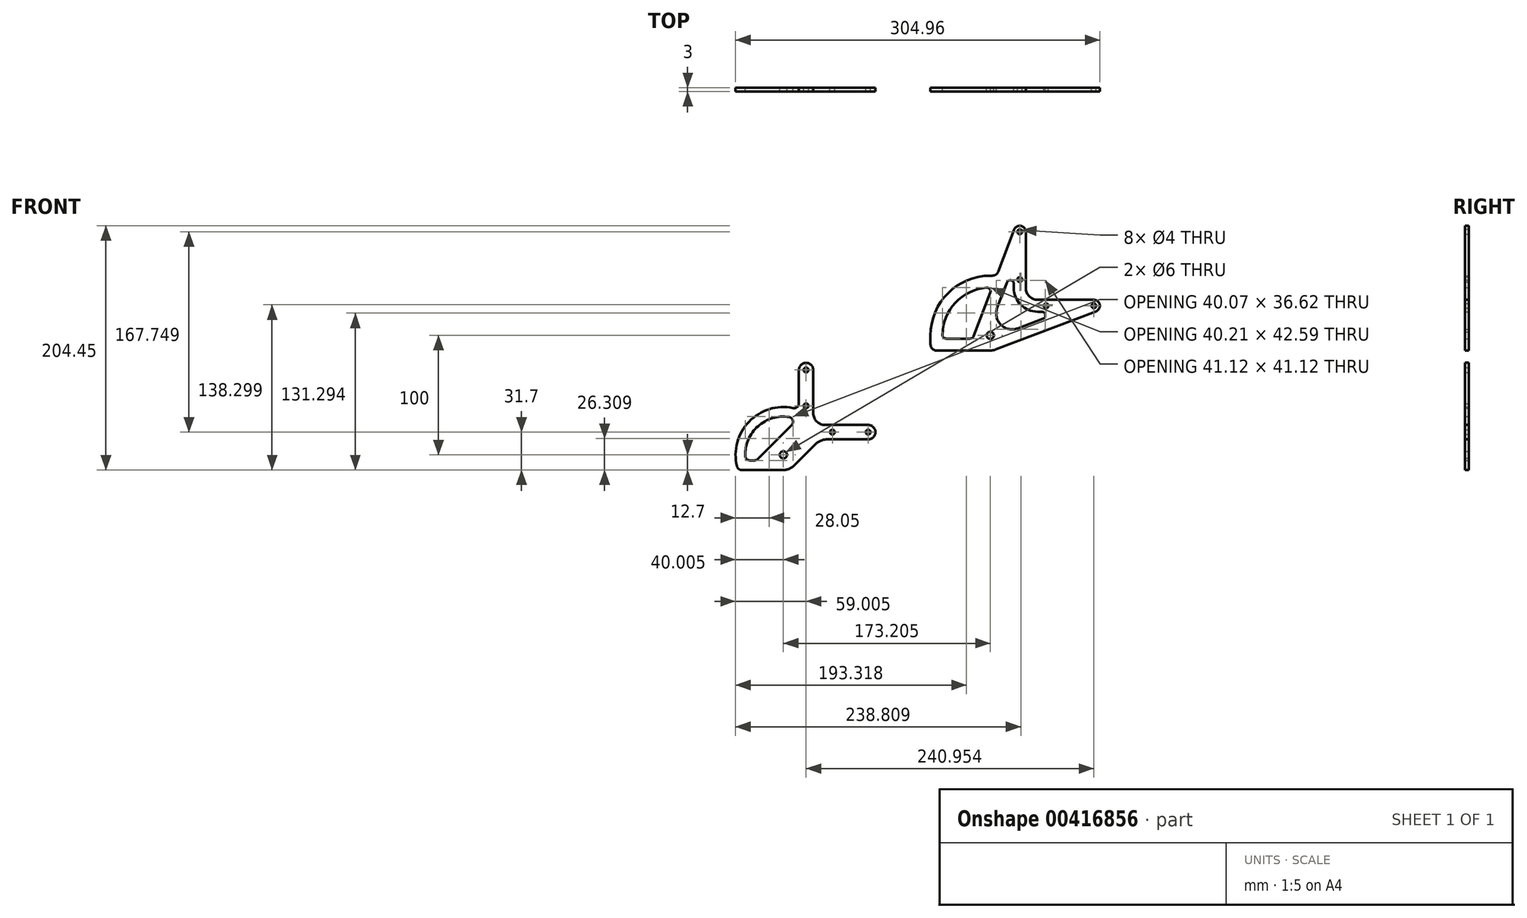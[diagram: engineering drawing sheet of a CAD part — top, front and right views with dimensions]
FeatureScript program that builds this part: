
annotation { "Feature Type Name" : "Feature", "Feature Type Description" : "" }
export const myFeature = defineFeature(function(context is Context, id is Id, definition is map)
    precondition{}
    {
        {
            var Q0;
            Q0=qCreatedBy(makeId("Front.planeOp"),FACE);
            var sketch = newSketch(context, id + "F0", { "sketchPlane" : qUnion([Q0])});
            skCircle(sketch, "E0", {"center": v(0, 0) * mm, "radius": 12.7 * mm, "construction": true});
            skLineSegment(sketch, "E1", {"start": v(0, 0) * mm, "end": v(0, -50) * mm, "construction": true});
            skCircle(sketch, "E2", {"center": v(0, -50) * mm, "radius": 6.35 * mm, "construction": true});
            skLineSegment(sketch, "E3", {"start": v(0, 0) * mm, "end": v(24.75, 24.75) * mm, "construction": true});
            skLineSegment(sketch, "E4", {"start": v(24.75, 24.75) * mm, "end": v(24.75, 86.75) * mm, "construction": true});
            skLineSegment(sketch, "E5", {"start": v(24.75, 24.75) * mm, "end": v(86.75, 24.75) * mm, "construction": true});
            skArc(sketch, "E6", {"start": v(0, 50) * mm, "mid": v(-35.36, 35.36) * mm, "end": v(-50, 0) * mm});
            skLineSegment(sketch, "E7.bottom", {"start": v(236.75, 36.75) * mm, "end": v(36.75, 36.75) * mm, "construction": true});
            skLineSegment(sketch, "E7.top", {"start": v(236.75, 12.75) * mm, "end": v(36.75, 12.75) * mm, "construction": true});
            skLineSegment(sketch, "E7.left", {"start": v(236.75, 36.75) * mm, "end": v(236.75, 12.75) * mm, "construction": true});
            skLineSegment(sketch, "E7.right", {"start": v(36.75, 36.75) * mm, "end": v(36.75, 12.75) * mm, "construction": true});
            skLineSegment(sketch, "E8.bottom", {"start": v(36.75, 36.75) * mm, "end": v(12.75, 36.75) * mm, "construction": true});
            skLineSegment(sketch, "E8.top", {"start": v(36.75, 156.75) * mm, "end": v(12.75, 156.75) * mm, "construction": true});
            skLineSegment(sketch, "E8.left", {"start": v(36.75, 36.75) * mm, "end": v(36.75, 156.75) * mm, "construction": true});
            skLineSegment(sketch, "E8.right", {"start": v(12.75, 36.75) * mm, "end": v(12.75, 156.75) * mm, "construction": true});
            skPoint(sketch, "E9", {"position": v(24.75, 36.75) * mm});
            skPoint(sketch, "E10", {"position": v(36.75, 24.75) * mm});
            skCircle(sketch, "E11", {"center": v(86.75, 24.75) * mm, "radius": 5 * mm, "construction": true});
            skCircle(sketch, "E12", {"center": v(24.75, 86.75) * mm, "radius": 5 * mm, "construction": true});
            skLineSegment(sketch, "E13", {"start": v(4.51, -11.87) * mm, "end": v(88.53, 20.08) * mm});
            skLineSegment(sketch, "E14.0", {"start": v(-44.08, 65.92) * mm, "end": v(56.26, 104.08) * mm, "construction": true});
            skLineSegment(sketch, "E15", {"start": v(6.65, 53.22) * mm, "end": v(20.08, 88.53) * mm});
            skLineSegment(sketch, "E16.0", {"start": v(29.75, 39.75) * mm, "end": v(29.75, 86.75) * mm});
            skLineSegment(sketch, "E17.0", {"start": v(39.75, 29.75) * mm, "end": v(86.75, 29.75) * mm});
            skArc(sketch, "E18.filletArc", {"start": v(29.75, 39.75) * mm, "mid": v(32.68, 32.68) * mm, "end": v(39.75, 29.75) * mm});
            skArc(sketch, "E19", {"start": v(20.08, 88.53) * mm, "mid": v(25.65, 91.67) * mm, "end": v(29.75, 86.75) * mm});
            skArc(sketch, "E20", {"start": v(86.75, 29.75) * mm, "mid": v(91.67, 25.65) * mm, "end": v(88.53, 20.08) * mm});
            skLineSegment(sketch, "E21", {"start": v(-45, -12.7) * mm, "end": v(0, -12.7) * mm});
            skLineSegment(sketch, "E22", {"start": v(0, 50) * mm, "end": v(1.98, 50) * mm});
            skArc(sketch, "E23", {"start": v(0, -12.7) * mm, "mid": v(2.3, -12.5) * mm, "end": v(4.51, -11.87) * mm});
            skLineSegment(sketch, "E24", {"start": v(-50, -7.7) * mm, "end": v(-50, 0) * mm});
            skLineSegment(sketch, "E25", {"start": v(61.22, 105.96) * mm, "end": v(91.42, 26.53) * mm, "construction": true});
            skLineSegment(sketch, "E26", {"start": v(-75.37, 54.03) * mm, "end": v(-50, -12.7) * mm, "construction": true});
            skCircle(sketch, "E27", {"center": v(24.75, 86.75) * mm, "radius": 2 * mm});
            skCircle(sketch, "E28", {"center": v(86.75, 24.75) * mm, "radius": 2 * mm});
            skCircle(sketch, "E29", {"center": v(46.75, 24.75) * mm, "radius": 2 * mm});
            skCircle(sketch, "E30", {"center": v(24.75, 46.75) * mm, "radius": 2 * mm});
            skCircle(sketch, "E31", {"center": v(0, 0) * mm, "radius": 3 * mm});
            skPoint(sketch, "E32.visualSharp", {"position": v(-50, -12.7) * mm});
            skArc(sketch, "E32.filletArc", {"start": v(-50, -7.7) * mm, "mid": v(-48.54, -11.24) * mm, "end": v(-45, -12.7) * mm});
            skPoint(sketch, "E33.visualSharp", {"position": v(5.43, 50) * mm});
            skArc(sketch, "E33.filletArc", {"start": v(1.98, 50) * mm, "mid": v(4.82, 50.88) * mm, "end": v(6.65, 53.22) * mm});
            skLineSegment(sketch, "E34.0", {"start": v(-37, -2.7) * mm, "end": v(-16.68, -2.7) * mm});
            skArc(sketch, "E34.2", {"start": v(-3, 39.89) * mm, "mid": v(-29.21, 27.32) * mm, "end": v(-40, 0.32) * mm});
            skLineSegment(sketch, "E35.0", {"start": v(23.03, 5.87) * mm, "end": v(44.27, 13.94) * mm});
            skLineSegment(sketch, "E36", {"start": v(0.04, 35.83) * mm, "end": v(-13.88, -0.77) * mm});
            skLineSegment(sketch, "E37.trimOffspring", {"start": v(-1.3, -2.7) * mm, "end": v(0, -2.7) * mm});
            skPoint(sketch, "E38.visualSharp", {"position": v(1.61, 39.97) * mm});
            skArc(sketch, "E38.filletArc", {"start": v(0.04, 35.83) * mm, "mid": v(-0.36, 38.7) * mm, "end": v(-3, 39.89) * mm});
            skPoint(sketch, "E39.visualSharp", {"position": v(-14.61, -2.7) * mm});
            skArc(sketch, "E39.filletArc", {"start": v(-16.68, -2.7) * mm, "mid": v(-14.98, -2.17) * mm, "end": v(-13.88, -0.77) * mm});
            skArc(sketch, "E40.filletArc", {"start": v(-40, 0.32) * mm, "mid": v(-39.13, -1.81) * mm, "end": v(-37, -2.7) * mm});
            skLineSegment(sketch, "E41.0", {"start": v(19.75, 39.75) * mm, "end": v(19.75, 43.2) * mm});
            skArc(sketch, "E41.1", {"start": v(19.75, 39.75) * mm, "mid": v(25.6, 25.6) * mm, "end": v(39.75, 19.75) * mm});
            skLineSegment(sketch, "E41.2", {"start": v(39.75, 19.75) * mm, "end": v(43.2, 19.75) * mm});
            skLineSegment(sketch, "E42.0", {"start": v(13.94, 44.27) * mm, "end": v(5.87, 23.03) * mm});
            skArc(sketch, "E43.filletArc", {"start": v(5.87, 23.03) * mm, "mid": v(8.9, 8.9) * mm, "end": v(23.03, 5.87) * mm});
            skPoint(sketch, "E44.visualSharp", {"position": v(59.53, 19.75) * mm});
            skArc(sketch, "E44.filletArc", {"start": v(44.27, 13.94) * mm, "mid": v(46.15, 17.3) * mm, "end": v(43.2, 19.75) * mm});
            skPoint(sketch, "E45.visualSharp", {"position": v(19.75, 59.53) * mm});
            skArc(sketch, "E45.filletArc", {"start": v(19.75, 43.2) * mm, "mid": v(17.3, 46.15) * mm, "end": v(13.94, 44.27) * mm});
            skLineSegment(sketch, "E46", {"start": v(0, 0) * mm, "end": v(50, 0) * mm, "construction": true});
            skCircle(sketch, "E47", {"center": v(50, 0) * mm, "radius": 6.35 * mm, "construction": true});
            skSolve(sketch);
        }
        {
            var Q0;
            Q0 = qSketchRegion(id + "F0", true);
            extrude(context, id + "F1", {"entities" : qUnion([Q0]), "depth" : 3 * mm});
        }
        {
            var Q0;
            Q0=qCreatedBy(makeId("Front.planeOp"),FACE);
            var sketch = newSketch(context, id + "F2", { "sketchPlane" : qUnion([Q0])});
            skLineSegment(sketch, "E48", {"start": v(-173.2, -100) * mm, "end": v(-173.2, -150) * mm, "construction": true});
            skCircle(sketch, "E49", {"center": v(-173.2, -150) * mm, "radius": 6.35 * mm, "construction": true});
            skLineSegment(sketch, "E50", {"start": v(-173.2, -100) * mm, "end": v(-154.2, -81) * mm, "construction": true});
            skLineSegment(sketch, "E51", {"start": v(-154.2, -81) * mm, "end": v(-154.2, -29) * mm, "construction": true});
            skLineSegment(sketch, "E52", {"start": v(-154.2, -81) * mm, "end": v(-102.2, -81) * mm, "construction": true});
            skArc(sketch, "E53", {"start": v(-165.02, -60.85) * mm, "mid": v(-202.02, -72.26) * mm, "end": v(-212.02, -109.67) * mm});
            skLineSegment(sketch, "E54.bottom", {"start": v(57.8, -69) * mm, "end": v(-142.2, -69) * mm, "construction": true});
            skLineSegment(sketch, "E54.top", {"start": v(57.8, -93) * mm, "end": v(-142.2, -93) * mm, "construction": true});
            skLineSegment(sketch, "E54.left", {"start": v(57.8, -69) * mm, "end": v(57.8, -93) * mm, "construction": true});
            skLineSegment(sketch, "E54.right", {"start": v(-142.2, -69) * mm, "end": v(-142.2, -93) * mm, "construction": true});
            skLineSegment(sketch, "E55.bottom", {"start": v(-142.2, -69) * mm, "end": v(-166.2, -69) * mm, "construction": true});
            skLineSegment(sketch, "E55.top", {"start": v(-142.2, 51) * mm, "end": v(-166.2, 51) * mm, "construction": true});
            skLineSegment(sketch, "E55.left", {"start": v(-142.2, -69) * mm, "end": v(-142.2, 51) * mm, "construction": true});
            skLineSegment(sketch, "E55.right", {"start": v(-166.2, -69) * mm, "end": v(-166.2, 51) * mm, "construction": true});
            skCircle(sketch, "E56", {"center": v(-102.2, -81) * mm, "radius": 6 * mm, "construction": true});
            skCircle(sketch, "E57", {"center": v(-154.2, -29) * mm, "radius": 6 * mm, "construction": true});
            skLineSegment(sketch, "E58.0", {"start": v(-148.2, -65) * mm, "end": v(-148.2, -29) * mm});
            skLineSegment(sketch, "E59.0", {"start": v(-138.2, -75) * mm, "end": v(-102.2, -75) * mm});
            skArc(sketch, "E60.filletArc", {"start": v(-148.2, -65) * mm, "mid": v(-145.28, -72.07) * mm, "end": v(-138.2, -75) * mm});
            skArc(sketch, "E61", {"start": v(-160.2, -29) * mm, "mid": v(-154.2, -23) * mm, "end": v(-148.2, -29) * mm});
            skArc(sketch, "E62", {"start": v(-102.2, -75) * mm, "mid": v(-96.2, -81) * mm, "end": v(-102.2, -87) * mm});
            skCircle(sketch, "E63", {"center": v(-154.2, -29) * mm, "radius": 2 * mm});
            skCircle(sketch, "E64", {"center": v(-102.2, -81) * mm, "radius": 2 * mm});
            skCircle(sketch, "E65", {"center": v(-132.2, -81) * mm, "radius": 2 * mm});
            skCircle(sketch, "E66", {"center": v(-154.2, -59) * mm, "radius": 2 * mm});
            skCircle(sketch, "E67", {"center": v(-173.2, -100) * mm, "radius": 3 * mm});
            skLineSegment(sketch, "E68", {"start": v(-173.2, -100) * mm, "end": v(-123.2, -100) * mm, "construction": true});
            skCircle(sketch, "E69", {"center": v(-123.2, -100) * mm, "radius": 6.35 * mm, "construction": true});
            skLineSegment(sketch, "E70", {"start": v(0, 0) * mm, "end": v(-173.2, -100) * mm, "construction": true});
            skLineSegment(sketch, "E71.0", {"start": v(-136.03, -87) * mm, "end": v(-102.2, -87) * mm});
            skLineSegment(sketch, "E72.0", {"start": v(-160.2, -69.04) * mm, "end": v(-160.2, -69) * mm});
            skLineSegment(sketch, "E73", {"start": v(-146.64, -91.4) * mm, "end": v(-164.22, -108.98) * mm});
            skLineSegment(sketch, "E74", {"start": v(-166.3, -75.13) * mm, "end": v(-194.7, -103.53) * mm});
            skPoint(sketch, "E75.visualSharp", {"position": v(-142.24, -87) * mm});
            skArc(sketch, "E75.filletArc", {"start": v(-136.03, -87) * mm, "mid": v(-141.77, -88.14) * mm, "end": v(-146.64, -91.4) * mm});
            skLineSegment(sketch, "E76", {"start": v(-208.14, -112.7) * mm, "end": v(-173.2, -112.7) * mm});
            skArc(sketch, "E77.0", {"start": v(-168.54, -68.34) * mm, "mid": v(-194.42, -76.04) * mm, "end": v(-205.2, -100.8) * mm});
            skLineSegment(sketch, "E78.0", {"start": v(-201.2, -104.7) * mm, "end": v(-197.52, -104.7) * mm});
            skPoint(sketch, "E79.visualSharp", {"position": v(-204.86, -104.7) * mm});
            skArc(sketch, "E79.filletArc", {"start": v(-205.2, -100.8) * mm, "mid": v(-203.99, -103.56) * mm, "end": v(-201.2, -104.7) * mm});
            skLineSegment(sketch, "E80.trimOffspring", {"start": v(-160.2, -56.93) * mm, "end": v(-160.2, -29) * mm});
            skPoint(sketch, "E81.visualSharp", {"position": v(-160.2, -62.17) * mm});
            skArc(sketch, "E81.filletArc", {"start": v(-165.02, -60.85) * mm, "mid": v(-161.68, -60.03) * mm, "end": v(-160.2, -56.93) * mm});
            skPoint(sketch, "E82.visualSharp", {"position": v(-161.42, -70.25) * mm});
            skArc(sketch, "E82.filletArc", {"start": v(-166.3, -75.13) * mm, "mid": v(-165.32, -71.04) * mm, "end": v(-168.54, -68.34) * mm});
            skPoint(sketch, "E83.visualSharp", {"position": v(-211.14, -112.7) * mm});
            skArc(sketch, "E83.filletArc", {"start": v(-212.02, -109.67) * mm, "mid": v(-210.6, -111.85) * mm, "end": v(-208.14, -112.7) * mm});
            skPoint(sketch, "E84.visualSharp", {"position": v(-195.87, -104.7) * mm});
            skArc(sketch, "E84.filletArc", {"start": v(-197.52, -104.7) * mm, "mid": v(-196, -104.4) * mm, "end": v(-194.7, -103.53) * mm});
            skCircle(sketch, "E85", {"center": v(-173.2, -100) * mm, "radius": 12.7 * mm, "construction": true});
            skArc(sketch, "E86", {"start": v(-173.2, -112.7) * mm, "mid": v(-168.35, -111.73) * mm, "end": v(-164.22, -108.98) * mm});
            skLineSegment(sketch, "E87", {"start": v(-215.19, -23) * mm, "end": v(-109.17, -23) * mm, "construction": true});
            skLineSegment(sketch, "E88", {"start": v(-213.2, -82.47) * mm, "end": v(-213.2, -123.4) * mm, "construction": true});
            skLineSegment(sketch, "E89", {"start": v(-96.2, -56.27) * mm, "end": v(-96.2, -101.46) * mm, "construction": true});
            skSolve(sketch);
        }
        {
            var Q0;
            Q0 = qSketchRegion(id + "F2", true);
            extrude(context, id + "F3", {"entities" : qUnion([Q0]), "depth" : 3 * mm});
        }
    });
